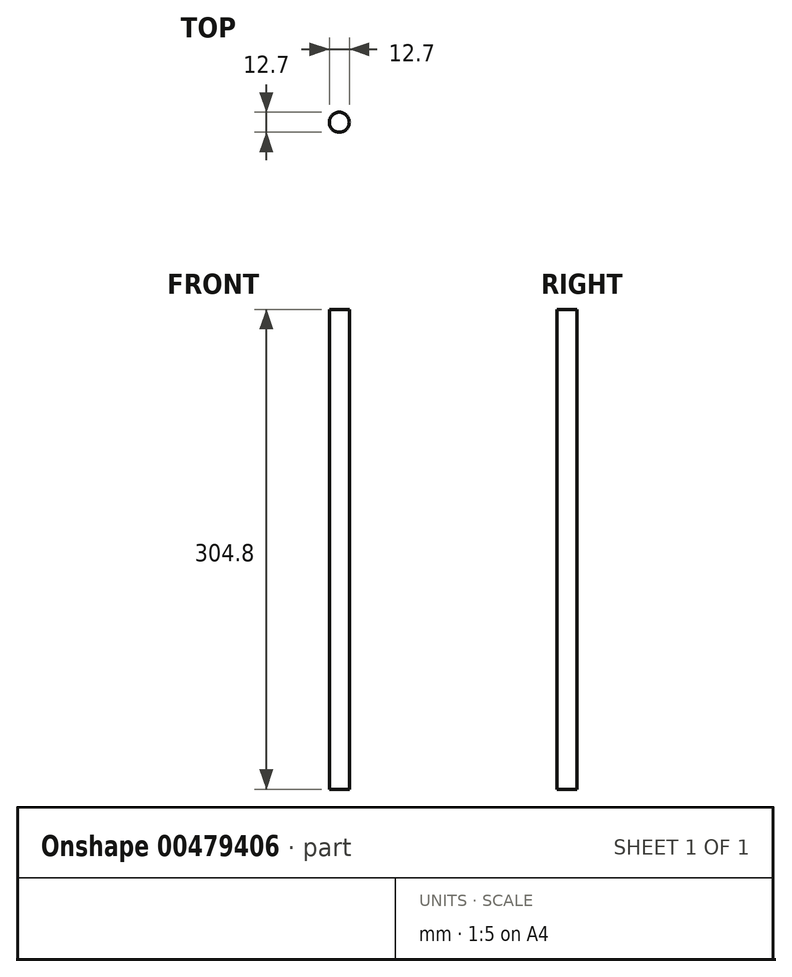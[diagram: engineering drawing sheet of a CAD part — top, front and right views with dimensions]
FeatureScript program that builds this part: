
annotation { "Feature Type Name" : "Feature", "Feature Type Description" : "" }
export const myFeature = defineFeature(function(context is Context, id is Id, definition is map)
    precondition{}
    {
        {
            var Q0;
            Q0=qCreatedBy(makeId("Top.planeOp"),FACE);
            var sketch = newSketch(context, id + "F0", { "sketchPlane" : qUnion([Q0])});
            skCircle(sketch, "E0", {"center": v(0, 0) * mm, "radius": 6.35 * mm});
            skSolve(sketch);
        }
        {
            var Q0;
            Q0 = qSketchRegion(id + "F0", true);
            extrude(context, id + "F1", {"entities" : qUnion([Q0]), "depth" : 304.8 * mm, "offsetDistance" : 25.4 * mm});
        }
    });
